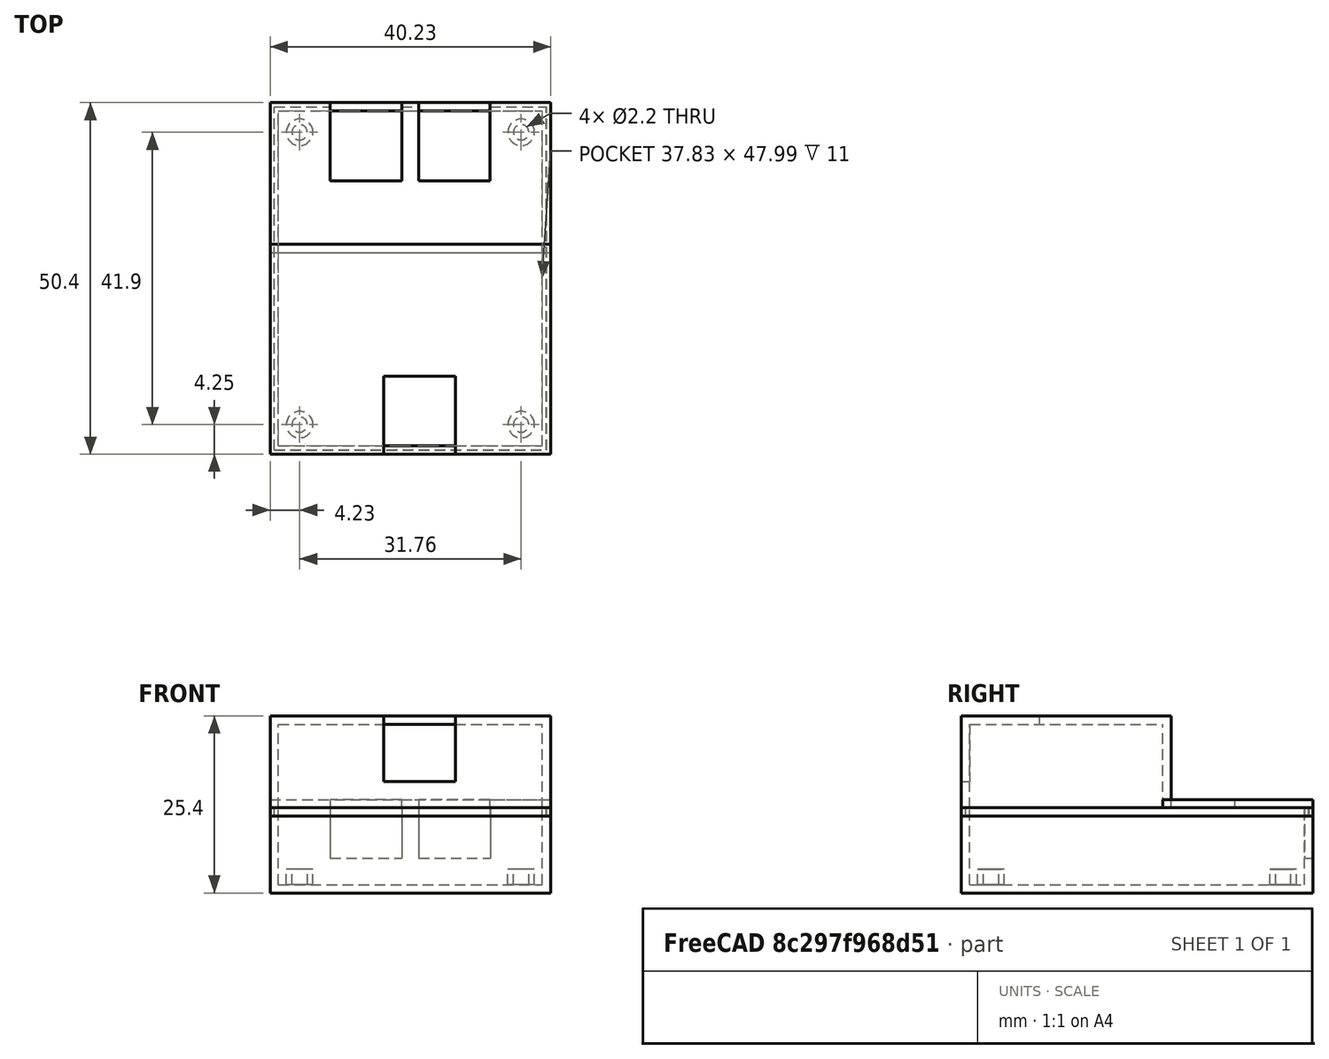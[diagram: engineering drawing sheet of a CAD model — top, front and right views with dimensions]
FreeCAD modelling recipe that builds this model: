
FCSTD DOCUMENT  (FreeCAD 0.20R)
Label: temp-module
License: All rights reserved
LicenseURL: http://en.wikipedia.org/wiki/All_rights_reserved
objects: Part::Box×16, Part::Cut×12, Part::FeaturePython×4, App::Part×3, PartDesign::FeatureBase×3, PartDesign::Body×3, App::VRMLObject×2, PartDesign::Thickness×2, Spreadsheet::Sheet×1, Part::Compound×1
note: 43 computed .brp shape members not serialized (recipe doc carries the construction recipe); baked Part::Feature solids carry a one-line shape summary decoded from their .brp

FEATURE [App::VRMLObject] can_atmega  label="can-atmega"
FEATURE [App::VRMLObject] temp_module  label="temp-module"
  Placement = pos=(0,-10.16,11) rot=(0,0,1;0rad)
FEATURE [App::Part] Part
  Group = -> [can_atmega,temp_module]
  Origin = -> Origin
FEATURE [Spreadsheet::Sheet] Spreadsheet  label="Global"
  cells = B2=bot_board_len; C2(bot_board_len)=36.83; D2(bot_case_len)==bot_board_len + 2 * border; E2=border; F2(border)=0.5; B3=bot_board_width; C3(bot_board_width)=46.99; D3(bot_case_width)==bot_board_width + 2 * border; B5=top_board_len; C5(top_board_len)=36.83; D5(top_case_len)==top_board_len + 2 * border; B6=top_board_width; C6(top_board_width)=26.67; D6(top_case_width)==top_board_width + 2 * border
FEATURE [Part::Box] Box014  label="Cube014"
  AttacherType = Attacher::AttachEngine3D
  Height = 12
  Length = 37.83
  Placement = pos=(-18.915,-23.995,8) rot=(0,0,1;0rad)
  Width = 27.67
  expr: .Placement.Base.x = -<<Global>>.top_case_len / 2
  expr: .Placement.Base.y = -<<Global>>.bot_case_width / 2
  expr: Length = <<Global>>.top_case_len
  expr: Width = <<Global>>.top_case_width
FEATURE [PartDesign::FeatureBase] BaseFeature
  BaseFeature = -> Box014
FEATURE [PartDesign::Thickness] Thickness002
  Base = -> BaseFeature [Face5]
  BaseFeature = -> BaseFeature
  Intersection = false
  Join = 1
  Mode = 0
  SupportTransform = false
  Value = 1.2
FEATURE [PartDesign::Body] Body
  BaseFeature = -> Box014
  Group = -> [BaseFeature,Thickness002]
  Origin = -> Origin004
  Placement = pos=(-18.915,-23.995,8) rot=(0,0,1;0rad)
  Tip = -> Thickness002
  expr: .Placement.Base.x = -<<Global>>.top_case_len / 2
  expr: .Placement.Base.y = -<<Global>>.bot_case_width / 2
FEATURE [Part::Box] Box015  label="Cube015"
  AttacherType = Attacher::AttachEngine3D
  Height = 1.2
  Length = 40.23
  Width = 21.52
  expr: Height = 1.2
  expr: Length = <<Global>>.bot_case_len + 2.4
  expr: Width = <<Global>>.bot_case_width - <<Global>>.top_case_width + 1.2
FEATURE [PartDesign::FeatureBase] BaseFeature002
  BaseFeature = -> Box015
FEATURE [PartDesign::Body] Body002
  BaseFeature = -> Box015
  Group = -> [BaseFeature002]
  Origin = -> Origin006
  Placement = pos=(-20.11,3.68,8) rot=(0,0,1;0rad)
  Tip = -> BaseFeature002
FEATURE [Part::Box] Box013  label="Cube013"
  AttacherType = Attacher::AttachEngine3D
  Height = 11
  Length = 37.83
  Placement = pos=(-18.915,-23.995,-3) rot=(0,0,1;0rad)
  Width = 47.99
  expr: .Placement.Base.x = -<<Global>>.bot_case_len / 2
  expr: .Placement.Base.y = -<<Global>>.bot_case_width / 2
  expr: Length = <<Global>>.bot_case_len
  expr: Width = <<Global>>.bot_case_width
FEATURE [PartDesign::FeatureBase] BaseFeature001
  BaseFeature = -> Box013
FEATURE [PartDesign::Thickness] Thickness003
  Base = -> BaseFeature001 [Face6]
  BaseFeature = -> BaseFeature001
  Intersection = false
  Join = 1
  Mode = 0
  SupportTransform = false
  Value = 1.2
FEATURE [PartDesign::Body] Body001
  BaseFeature = -> Box013
  Group = -> [BaseFeature001,Thickness003]
  Origin = -> Origin005
  Placement = pos=(-18.915,-23.995,-3) rot=(0,0,1;0rad)
  Tip = -> Thickness003
  expr: .Placement.Base.x = -<<Global>>.bot_case_len / 2
  expr: .Placement.Base.y = -<<Global>>.bot_case_width / 2
FEATURE [Part::Box] Box017  label="Cube017"
  AttacherType = Attacher::AttachEngine3D
  Height = 1.2
  Length = 37.83
  Placement = pos=(-18.91,-24,0) rot=(0,0,1;0rad)
  Width = 47.99
  expr: .Placement.Base.x = -<<Global>>.bot_case_len / 2
  expr: .Placement.Base.y = -<<Global>>.bot_case_width / 2
  expr: Length = <<Global>>.bot_case_len
  expr: Width = <<Global>>.bot_case_width
FEATURE [Part::Box] Box018  label="Cube018"
  AttacherType = Attacher::AttachEngine3D
  Height = 1.2
  Length = 39.03
  Placement = pos=(-19.52,-24.6,0) rot=(0,0,1;0rad)
  Width = 49.19
  expr: .Placement.Base.x = -(<<Global>>.bot_case_len + 1.2) / 2
  expr: .Placement.Base.y = -(<<Global>>.bot_case_width + 1.2) / 2
  expr: Length = <<Global>>.bot_case_len + 1.2
  expr: Width = <<Global>>.bot_case_width + 1.2
FEATURE [Part::Cut] Cut001
  Base = -> Box018
  Tool = -> Box017
FEATURE [Part::Box] Box021  label="Cube021"
  AttacherType = Attacher::AttachEngine3D
  Height = 1.2
  Length = 37.83
  Placement = pos=(-18.91,-24,0) rot=(0,0,1;0rad)
  Width = 47.99
  expr: .Placement.Base.x = -<<Global>>.bot_case_len / 2
  expr: .Placement.Base.y = -<<Global>>.bot_case_width / 2
  expr: Length = <<Global>>.bot_case_len
  expr: Width = <<Global>>.bot_case_width
FEATURE [Part::Box] Box022  label="Cube022"
  AttacherType = Attacher::AttachEngine3D
  Height = 1.2
  Length = 40.23
  Placement = pos=(-20.11,-25.2,0) rot=(0,0,1;0rad)
  Width = 50.39
  expr: .Placement.Base.x = -(<<Global>>.bot_case_len + 2.4) / 2
  expr: .Placement.Base.y = -(<<Global>>.bot_case_width + 2.4) / 2
  expr: Length = <<Global>>.bot_case_len + 2.4
  expr: Width = <<Global>>.bot_case_width + 2.4
FEATURE [Part::Cut] Cut003
  Base = -> Box022
  Tool = -> Box021
FEATURE [Part::Cut] Cut004
  Base = -> Cut003
  Placement = pos=(0,0,6.8) rot=(0,0,1;0rad)
  Tool = -> Cut001
FEATURE [Part::Box] Box025  label="Cube025"
  AttacherType = Attacher::AttachEngine3D
  Height = 1.2
  Length = 37.83
  Placement = pos=(-18.91,-24,0) rot=(0,0,1;0rad)
  Width = 47.99
  expr: .Placement.Base.x = -<<Global>>.bot_case_len / 2
  expr: .Placement.Base.y = -<<Global>>.bot_case_width / 2
  expr: Length = <<Global>>.bot_case_len
  expr: Width = <<Global>>.bot_case_width
FEATURE [Part::Box] Box026  label="Cube026"
  AttacherType = Attacher::AttachEngine3D
  Height = 1.2
  Length = 38.98
  Placement = pos=(-19.49,-24.57,0) rot=(0,0,1;0rad)
  Width = 49.14
  expr: .Placement.Base.x = -(<<Global>>.bot_case_len + 1.15) / 2
  expr: .Placement.Base.y = -(<<Global>>.bot_case_width + 1.15) / 2
  expr: Length = <<Global>>.bot_case_len + 1.15
  expr: Width = <<Global>>.bot_case_width + 1.15
FEATURE [Part::Box] Box027  label="Cube027"
  AttacherType = Attacher::AttachEngine3D
  Height = 1.2
  Length = 37.83
  Placement = pos=(-18.91,-24,0) rot=(0,0,1;0rad)
  Width = 47.99
  expr: .Placement.Base.x = -<<Global>>.bot_case_len / 2
  expr: .Placement.Base.y = -<<Global>>.bot_case_width / 2
  expr: Length = <<Global>>.bot_case_len
  expr: Width = <<Global>>.bot_case_width
FEATURE [Part::Box] Box028  label="Cube028"
  AttacherType = Attacher::AttachEngine3D
  Height = 1.2
  Length = 40.25
  Placement = pos=(-20.125,-25.205,0) rot=(0,0,1;0rad)
  Width = 50.41
  expr: .Placement.Base.x = -(<<Global>>.bot_case_len + 2.42) / 2
  expr: .Placement.Base.y = -(<<Global>>.bot_case_width + 2.42) / 2
  expr: Length = <<Global>>.bot_case_len + 2.42
  expr: Width = <<Global>>.bot_case_width + 2.42
FEATURE [Part::Cut] Cut006
  Base = -> Box026
  Tool = -> Box025
FEATURE [Part::Cut] Cut007
  Base = -> Box028
  Tool = -> Box027
FEATURE [Part::Cut] Cut008
  Base = -> Cut007
  Placement = pos=(0,0,6.8) rot=(0,0,1;0rad)
  Tool = -> Cut006
FEATURE [Part::Cut] Cut
  Base = -> Body001
  Tool = -> Cut008
FEATURE [Part::Box] Box  label="Cube"
  AttacherType = Attacher::AttachEngine3D
  Height = 13
  Length = 10.25
  Placement = pos=(1.2,14,0.79) rot=(0,0,1;0rad)
  Width = 12
FEATURE [Part::Cut] Cut009
  Base = -> Cut
  Tool = -> Box
FEATURE [Part::Box] Box029  label="Cube029"
  AttacherType = Attacher::AttachEngine3D
  Height = 13
  Length = 10.25
  Placement = pos=(-11.49,14,0.79) rot=(0,0,1;0rad)
  Width = 12
FEATURE [Part::Cut] Cut010
  Base = -> Cut009
  Tool = -> Box029
FEATURE [Part::Box] Box030  label="Cube030"
  AttacherType = Attacher::AttachEngine3D
  Height = 13
  Length = 10.25
  Placement = pos=(-11.49,14,0.79) rot=(0,0,1;0rad)
  Width = 12
FEATURE [Part::Compound] Compound
  Links = -> [Body,Body002,Cut004]
FEATURE [Part::Cut] Cut011
  Base = -> Compound
  Tool = -> Box030
FEATURE [Part::Box] Box031  label="Cube031"
  AttacherType = Attacher::AttachEngine3D
  Height = 13
  Length = 10.25
  Placement = pos=(1.19,14,0.79) rot=(0,0,1;0rad)
  Width = 12
FEATURE [Part::Cut] Cut012
  Base = -> Cut011
  Tool = -> Box031
FEATURE [Part::Box] Box032  label="Cube032"
  AttacherType = Attacher::AttachEngine3D
  Height = 13
  Length = 10.25
  Placement = pos=(-3.81,-26,11.79) rot=(0,0,1;0rad)
  Width = 12
FEATURE [Part::Cut] Cut013
  Base = -> Cut012
  Tool = -> Box032
FEATURE [App::Part] Part004
  Group = -> [Box014,Body,Box015,Body002,Box018,Box017,Cut001,Box021,Box022,Cut003,Cut004,Box030,Compound,Cut011,Box031,Cut012,Box032,Cut013]
  Origin = -> Origin007
FEATURE [Part::FeaturePython] Tube  # WARN: FeaturePython — macro-defined, semantics opaque (R4)
  AttacherType = Attacher::AttachEngine3D
  Height = 2.21
  InnerRadius = 1.1
  OuterRadius = 1.9
  Placement = pos=(-15.88,20.95,-3) rot=(0,0,1;0rad)
FEATURE [Part::FeaturePython] Tube001  # WARN: FeaturePython — macro-defined, semantics opaque (R4)
  AttacherType = Attacher::AttachEngine3D
  Height = 2.21
  InnerRadius = 1.1
  OuterRadius = 1.9
  Placement = pos=(15.88,20.95,-3) rot=(0,0,1;0rad)
FEATURE [Part::FeaturePython] Tube002  # WARN: FeaturePython — macro-defined, semantics opaque (R4)
  AttacherType = Attacher::AttachEngine3D
  Height = 2.21
  InnerRadius = 1.1
  OuterRadius = 1.9
  Placement = pos=(15.88,-20.95,-3) rot=(0,0,1;0rad)
FEATURE [Part::FeaturePython] Tube003  # WARN: FeaturePython — macro-defined, semantics opaque (R4)
  AttacherType = Attacher::AttachEngine3D
  Height = 2.21
  InnerRadius = 1.1
  OuterRadius = 1.9
  Placement = pos=(-15.88,-20.95,-3) rot=(0,0,1;0rad)
FEATURE [App::Part] Part003
  Group = -> [Body001,Box013,Box026,Box027,Box025,Cut007,Box028,Cut006,Cut008,Cut,Box,Cut009,Box029,Cut010,Tube,Tube001,Tube002,Tube003]
  Origin = -> Origin003
